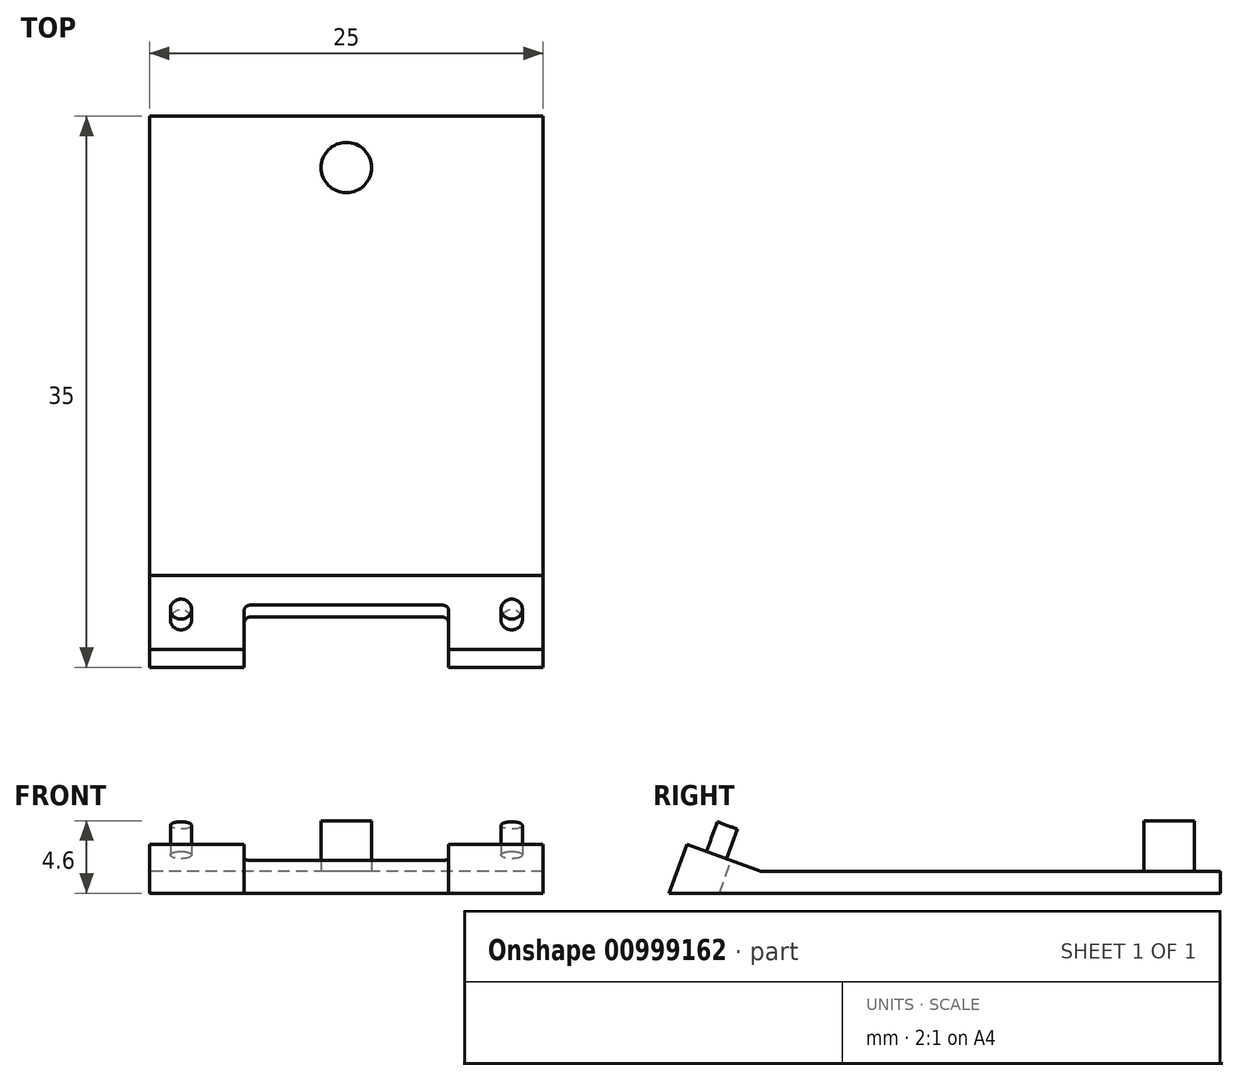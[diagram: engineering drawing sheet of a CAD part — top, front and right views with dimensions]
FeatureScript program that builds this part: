
annotation { "Feature Type Name" : "Feature", "Feature Type Description" : "" }
export const myFeature = defineFeature(function(context is Context, id is Id, definition is map)
    precondition{}
    {
        {
            assignVariable(context, id + "F0", {"name" : "CAM_WIDTH", "anyValue" : 25});
        }
        {
            var Q0;
            Q0=qCreatedBy(makeId("Right.planeOp"),FACE);
            var sketch = newSketch(context, id + "F1", { "sketchPlane" : qUnion([Q0])});
            skLineSegment(sketch, "E0", {"start": v(35, 0) * mm, "end": v(0, 0) * mm});
            skLineSegment(sketch, "E1", {"start": v(0, 0) * mm, "end": v(1.13, 3.11) * mm});
            skLineSegment(sketch, "E2", {"start": v(1.13, 3.11) * mm, "end": v(5.83, 1.4) * mm});
            skLineSegment(sketch, "E3", {"start": v(5.83, 1.4) * mm, "end": v(35, 1.4) * mm});
            skLineSegment(sketch, "E4", {"start": v(35, 1.4) * mm, "end": v(35, 0) * mm});
            skSolve(sketch);
        }
        {
            var Q0;
            Q0=makeQuery(id+"F1.imprint","IMPRINT",FACE,{"disambiguationData":[TD([[makeQuery(id+"F1.imprint","IMPRINT",EDGE,{"derivedFrom":sQuery(id+"F1.wireOp",EDGE,"E0")}),-1.0]])]});
            extrude(context, id + "F2", {"entities" : qUnion([Q0]), "depth" : (getVariable(context, 'CAM_WIDTH')) * mm, "offsetDistance" : 25 * mm});
        }
        {
            var Q0;
            Q0=makeQuery(id+"F2.opExtrude","SWEPT_FACE",FACE,{"disambiguationData":[OSD([sQuery(id+"F1.wireOp",EDGE,"E2")])]});
            var sketch = newSketch(context, id + "F3", { "sketchPlane" : qUnion([Q0])});
            skLineSegment(sketch, "E5.bottom", {"start": v(19, 0) * mm, "end": v(6, 0) * mm});
            skLineSegment(sketch, "E5.top", {"start": v(18.6, 3) * mm, "end": v(6.4, 3) * mm});
            skLineSegment(sketch, "E5.left", {"start": v(19, 0) * mm, "end": v(19, 2.6) * mm});
            skLineSegment(sketch, "E5.right", {"start": v(6, 0) * mm, "end": v(6, 2.6) * mm});
            skPoint(sketch, "E6", {"position": v(12.5, 0) * mm});
            skPoint(sketch, "E7.visualSharp", {"position": v(19, 3) * mm});
            skArc(sketch, "E7.filletArc", {"start": v(19, 2.6) * mm, "mid": v(18.88, 2.88) * mm, "end": v(18.6, 3) * mm});
            skPoint(sketch, "E8.visualSharp", {"position": v(6, 3) * mm});
            skArc(sketch, "E8.filletArc", {"start": v(6.4, 3) * mm, "mid": v(6.12, 2.88) * mm, "end": v(6, 2.6) * mm});
            skSolve(sketch);
        }
        {
            var Q0;
            Q0 = qSketchRegion(id + "F3", true);
            extrude(context, id + "F4", {"entities" : qUnion([Q0]), "operationType" : NewBodyOperationType.REMOVE, "endBound" : BoundingType.UP_TO_NEXT, "oppositeDirection" : true, "depth" : 25 * mm, "offsetDistance" : 25 * mm});
        }
        {
            var Q0;
            Q0=makeQuery(id+"F2.opExtrude","SWEPT_FACE",FACE,{"disambiguationData":[OSD([sQuery(id+"F1.wireOp",EDGE,"E2")])]});
            var sketch = newSketch(context, id + "F5", { "sketchPlane" : qUnion([Q0])});
            skCircle(sketch, "E9", {"center": v(23, 2) * mm, "radius": 0.68 * mm});
            skCircle(sketch, "E10", {"center": v(2, 2) * mm, "radius": 0.68 * mm});
            skLineSegment(sketch, "E11", {"start": v(2, 2) * mm, "end": v(0, 2) * mm, "construction": true});
            skLineSegment(sketch, "E12", {"start": v(23, 2) * mm, "end": v(25, 2) * mm, "construction": true});
            skSolve(sketch);
        }
        {
            var Q0;
            Q0=makeQuery(id+"F5.imprint","IMPRINT",FACE,{"disambiguationData":[TD([[makeQuery(id+"F5.imprint","IMPRINT",EDGE,{"derivedFrom":sQuery(id+"F5.wireOp",EDGE,"E9")}),1.0]])]});
            var Q1;
            Q1=makeQuery(id+"F5.imprint","IMPRINT",FACE,{"disambiguationData":[TD([[makeQuery(id+"F5.imprint","IMPRINT",EDGE,{"derivedFrom":sQuery(id+"F5.wireOp",EDGE,"E10")}),1.0]])]});
            extrude(context, id + "F6", {"entities" : qUnion([Q0, Q1]), "operationType" : NewBodyOperationType.ADD, "depth" : 2 * mm, "offsetDistance" : 25 * mm});
        }
        {
            var Q0;
            Q0=makeQuery(id+"F2.opExtrude","SWEPT_FACE",FACE,{"disambiguationData":[OSD([sQuery(id+"F1.wireOp",EDGE,"E3")])]});
            var sketch = newSketch(context, id + "F7", { "sketchPlane" : qUnion([Q0])});
            skCircle(sketch, "E13", {"center": v(12.5, 31.74) * mm, "radius": 1.6 * mm});
            skLineSegment(sketch, "E14", {"start": v(12.5, 31.74) * mm, "end": v(0, 31.74) * mm, "construction": true});
            skLineSegment(sketch, "E15", {"start": v(12.5, 31.74) * mm, "end": v(25, 31.74) * mm, "construction": true});
            skSolve(sketch);
        }
        {
            var Q0;
            Q0=makeQuery(id+"F7.imprint","IMPRINT",FACE,{"disambiguationData":[TD([[makeQuery(id+"F7.imprint","IMPRINT",EDGE,{"derivedFrom":sQuery(id+"F7.wireOp",EDGE,"E13")}),1.0]])]});
            var Q1;
            Q1=sQuery(id+"F7.wireOp",EDGE,"E13");
            extrude(context, id + "F8", {"entities" : qUnion([Q0]), "operationType" : NewBodyOperationType.ADD, "surfaceEntities" : qUnion([Q1]), "depth" : 3.2 * mm, "offsetDistance" : 25 * mm});
        }
    });
